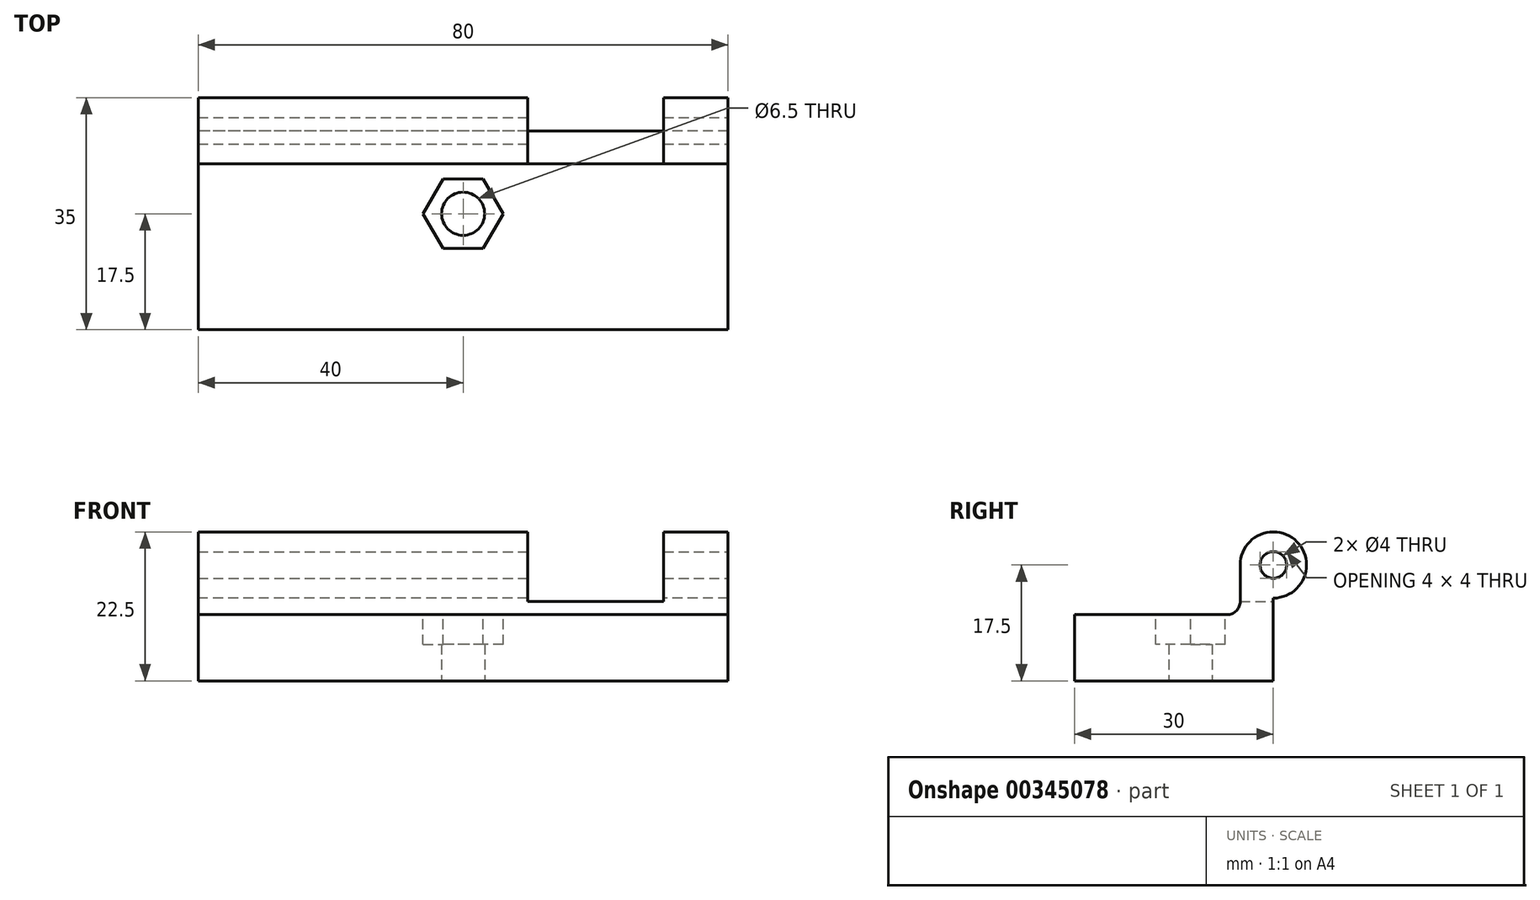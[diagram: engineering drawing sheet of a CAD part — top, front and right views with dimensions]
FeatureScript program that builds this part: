
annotation { "Feature Type Name" : "Feature", "Feature Type Description" : "" }
export const myFeature = defineFeature(function(context is Context, id is Id, definition is map)
    precondition{}
    {
        {
            var Q0;
            Q0=qCreatedBy(makeId("Right.planeOp"),FACE);
            var sketch = newSketch(context, id + "F0", { "sketchPlane" : qUnion([Q0])});
            skLineSegment(sketch, "E0", {"start": v(-17.5, 0) * mm, "end": v(12.5, 0) * mm});
            skLineSegment(sketch, "E1", {"start": v(12.5, 0) * mm, "end": v(12.5, 12.5) * mm});
            skLineSegment(sketch, "E2", {"start": v(7.5, 17.5) * mm, "end": v(7.5, 10) * mm});
            skLineSegment(sketch, "E3", {"start": v(7.5, 10) * mm, "end": v(-17.5, 10) * mm});
            skLineSegment(sketch, "E4", {"start": v(-17.5, 10) * mm, "end": v(-17.5, 0) * mm});
            skArc(sketch, "E5", {"start": v(12.5, 12.5) * mm, "mid": v(16.04, 21.04) * mm, "end": v(7.5, 17.5) * mm});
            skSolve(sketch);
        }
        {
            var Q0;
            Q0 = qSketchRegion(id + "F0", true);
            extrude(context, id + "F1", {"entities" : qUnion([Q0]), "endBound" : BoundingType.SYMMETRIC, "depth" : 80 * mm});
        }
        {
            var Q0;
            Q0=makeQuery(id+"F1.opExtrude","CAP_FACE",FACE,{"disambiguationData":[OSD([sQuery(id+"F0.wireOp",EDGE,"E0"),sQuery(id+"F0.wireOp",EDGE,"E1"),sQuery(id+"F0.wireOp",EDGE,"E2"),sQuery(id+"F0.wireOp",EDGE,"E3"),sQuery(id+"F0.wireOp",EDGE,"E4"),sQuery(id+"F0.wireOp",EDGE,"E5")])],"isStart":false});
            var sketch = newSketch(context, id + "F2", { "sketchPlane" : qUnion([Q0])});
            skCircle(sketch, "E6", {"center": v(12.5, 17.5) * mm, "radius": 2 * mm});
            skSolve(sketch);
        }
        {
            var Q0;
            Q0 = qSketchRegion(id + "F2", true);
            extrude(context, id + "F3", {"entities" : qUnion([Q0]), "operationType" : NewBodyOperationType.REMOVE, "endBound" : BoundingType.THROUGH_ALL, "oppositeDirection" : true, "depth" : 25 * mm});
        }
        {
            var Q0;
            Q0=makeQuery(id+"F1.opExtrude","SWEPT_EDGE",EDGE,{"disambiguationData":[OSD([sQuery(id+"F0.wireOp",EDGE,"E2"),sQuery(id+"F0.wireOp",EDGE,"E3")])]});
            fillet(context, id + "F4", {"entities" : qUnion([Q0]), "radius" : 2 * mm, "tangentPropagation" : true, "allowEdgeOverflow" : false});
        }
        {
            var Q0;
            Q0=makeQuery(id+"F1.opExtrude","SWEPT_FACE",FACE,{"disambiguationData":[OSD([sQuery(id+"F0.wireOp",EDGE,"E3")])]});
            cPlane(context, id + "F5", {"entities" : qUnion([Q0]), "cplaneType" : CPlaneType.OFFSET, "offset" : 2 * mm, "width" : 150 * mm, "height" : 150 * mm});
        }
        {
            var Q0;
            Q0=qCreatedBy(id+"F5.planeOp",FACE);
            var sketch = newSketch(context, id + "F6", { "sketchPlane" : qUnion([Q0])});
            skLineSegment(sketch, "E7.bottom", {"start": v(30.25, 7.5) * mm, "end": v(9.75, 7.5) * mm});
            skLineSegment(sketch, "E7.top", {"start": v(30.25, 19.5) * mm, "end": v(9.75, 19.5) * mm});
            skLineSegment(sketch, "E7.left", {"start": v(30.25, 7.5) * mm, "end": v(30.25, 19.5) * mm});
            skLineSegment(sketch, "E7.right", {"start": v(9.75, 7.5) * mm, "end": v(9.75, 19.5) * mm});
            skSolve(sketch);
        }
        {
            var Q0;
            Q0 = qSketchRegion(id + "F6", true);
            extrude(context, id + "F7", {"entities" : qUnion([Q0]), "operationType" : NewBodyOperationType.REMOVE, "endBound" : BoundingType.THROUGH_ALL, "depth" : 25 * mm});
        }
        {
            var Q0;
            Q0=makeQuery(id+"F1.opExtrude","SWEPT_FACE",FACE,{"disambiguationData":[OSD([sQuery(id+"F0.wireOp",EDGE,"E3")])]});
            var sketch = newSketch(context, id + "F8", { "sketchPlane" : qUnion([Q0])});
            skCircle(sketch, "E8.cCircle", {"center": v(0, 0) * mm, "radius": 5.25 * mm, "construction": true});
            skLineSegment(sketch, "E8.0", {"start": v(3.03, -5.25) * mm, "end": v(-3.03, -5.25) * mm});
            skLineSegment(sketch, "E8.1", {"start": v(-3.03, -5.25) * mm, "end": v(-6.06, 0) * mm});
            skLineSegment(sketch, "E8.2", {"start": v(-6.06, 0) * mm, "end": v(-3.03, 5.25) * mm});
            skLineSegment(sketch, "E8.3", {"start": v(-3.03, 5.25) * mm, "end": v(3.03, 5.25) * mm});
            skLineSegment(sketch, "E8.4", {"start": v(3.03, 5.25) * mm, "end": v(6.06, 0) * mm});
            skLineSegment(sketch, "E8.5", {"start": v(6.06, 0) * mm, "end": v(3.03, -5.25) * mm});
            skPoint(sketch, "E8.0.midPoint", {"position": v(0, -5.25) * mm});
            skLineSegment(sketch, "E9", {"start": v(-6.06, 0) * mm, "end": v(6.06, 0) * mm, "construction": true});
            skSolve(sketch);
        }
        {
            var Q0;
            Q0 = qSketchRegion(id + "F8", true);
            extrude(context, id + "F9", {"entities" : qUnion([Q0]), "operationType" : NewBodyOperationType.REMOVE, "oppositeDirection" : true, "depth" : 4.5 * mm});
        }
        {
            var Q0;
            Q0=makeQuery(id+"F1.opExtrude","SWEPT_FACE",FACE,{"disambiguationData":[OSD([sQuery(id+"F0.wireOp",EDGE,"E0")])]});
            var sketch = newSketch(context, id + "F10", { "sketchPlane" : qUnion([Q0])});
            skCircle(sketch, "E10", {"center": v(0, 0) * mm, "radius": 3.25 * mm});
            skSolve(sketch);
        }
        {
            var Q0;
            Q0=makeQuery(id+"F10.imprint","IMPRINT",FACE,{"disambiguationData":[TD([[makeQuery(id+"F10.imprint","IMPRINT",EDGE,{"derivedFrom":sQuery(id+"F10.wireOp",EDGE,"E10")}),1.0]])]});
            extrude(context, id + "F11", {"entities" : qUnion([Q0]), "operationType" : NewBodyOperationType.REMOVE, "endBound" : BoundingType.THROUGH_ALL, "oppositeDirection" : true, "depth" : 25 * mm});
        }
    });
